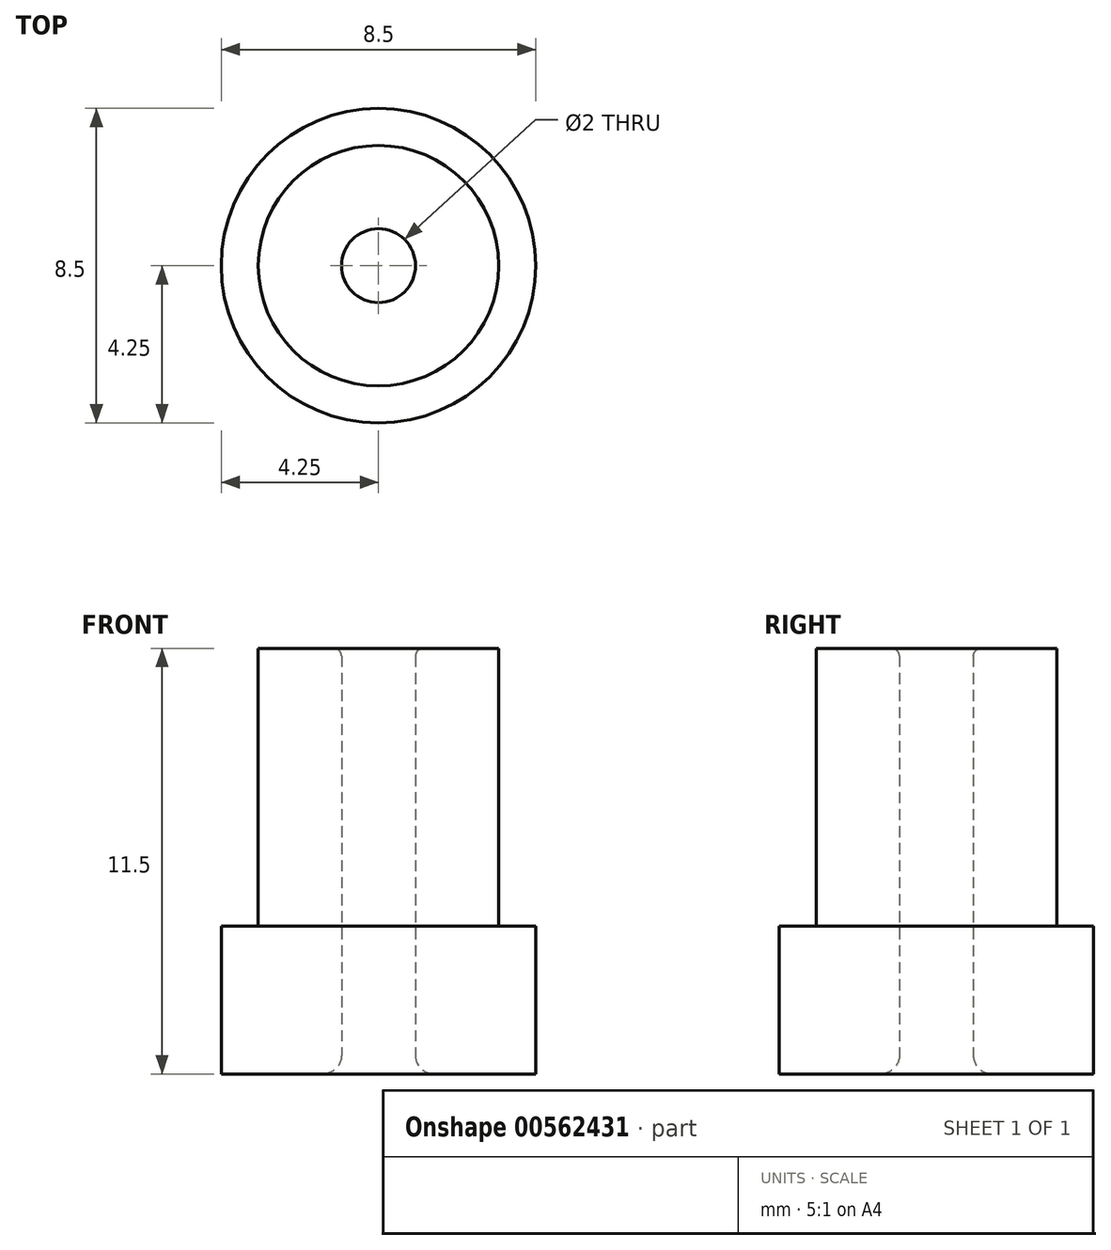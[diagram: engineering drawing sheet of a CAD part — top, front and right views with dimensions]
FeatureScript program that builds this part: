
annotation { "Feature Type Name" : "Feature", "Feature Type Description" : "" }
export const myFeature = defineFeature(function(context is Context, id is Id, definition is map)
    precondition{}
    {
        {
            var Q0;
            Q0=qCreatedBy(makeId("Top.planeOp"),FACE);
            var sketch = newSketch(context, id + "F0", { "sketchPlane" : qUnion([Q0])});
            skCircle(sketch, "E0", {"center": v(0, 0) * mm, "radius": 1 * mm});
            skCircle(sketch, "E1", {"center": v(0, 0) * mm, "radius": 3.25 * mm});
            skCircle(sketch, "E2", {"center": v(0, 0) * mm, "radius": 4.25 * mm});
            skSolve(sketch);
        }
        {
            var Q0;
            Q0=makeQuery(id+"F0.imprint","IMPRINT",FACE,{"disambiguationData":[TD([[makeQuery(id+"F0.imprint","IMPRINT",EDGE,{"derivedFrom":sQuery(id+"F0.wireOp",EDGE,"E0")}),-1.0]])]});
            extrude(context, id + "F1", {"entities" : qUnion([Q0]), "depth" : 11.5 * mm, "offsetDistance" : 25 * mm});
        }
        {
            var Q0;
            Q0=makeQuery(id+"F0.imprint","IMPRINT",FACE,{"disambiguationData":[TD([[makeQuery(id+"F0.imprint","IMPRINT",EDGE,{"derivedFrom":sQuery(id+"F0.wireOp",EDGE,"E1")}),-1.0]])]});
            extrude(context, id + "F2", {"entities" : qUnion([Q0]), "operationType" : NewBodyOperationType.ADD, "depth" : 4 * mm, "offsetDistance" : 25 * mm});
        }
        {
            var Q0;
            Q0=makeQuery(id+"F1.opExtrude","CAP_EDGE",EDGE,{"disambiguationData":[OSD([sQuery(id+"F0.wireOp",EDGE,"E0")])],"isStart":false});
            fillet(context, id + "F3", {"entities" : qUnion([Q0]), "radius" : .2 * mm, "tangentPropagation" : true, "allowEdgeOverflow" : false});
        }
        {
            var Q0;
            Q0=makeQuery(id+"F1.opExtrude","CAP_EDGE",EDGE,{"disambiguationData":[OSD([sQuery(id+"F0.wireOp",EDGE,"E0")])],"isStart":true});
            fillet(context, id + "F4", {"entities" : qUnion([Q0]), "radius" : .5 * mm, "tangentPropagation" : true, "allowEdgeOverflow" : false});
        }
    });
